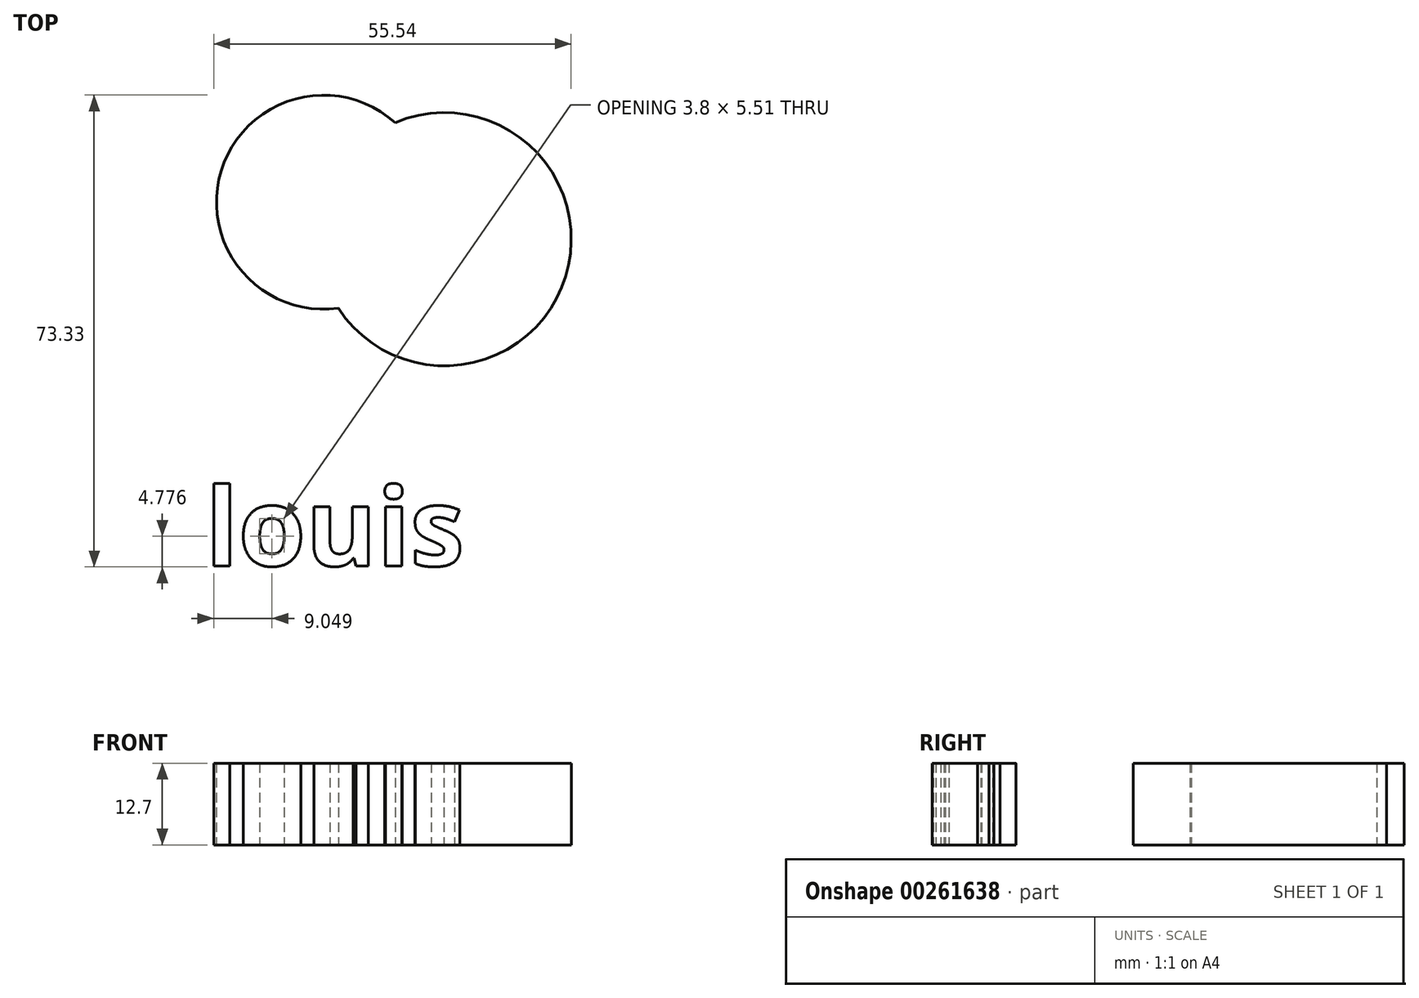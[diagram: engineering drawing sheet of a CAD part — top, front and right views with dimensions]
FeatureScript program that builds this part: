
annotation { "Feature Type Name" : "Feature", "Feature Type Description" : "" }
export const myFeature = defineFeature(function(context is Context, id is Id, definition is map)
    precondition{}
    {
        {
            var Q0;
            Q0=qCreatedBy(makeId("Top.planeOp"),FACE);
            var sketch = newSketch(context, id + "F0", { "sketchPlane" : qUnion([Q0])});
            skCircle(sketch, "E0", {"center": v(-6.81, 12.7) * mm, "radius": 19.68 * mm});
            skCircle(sketch, "E1", {"center": v(-25.62, 18.47) * mm, "radius": 16.63 * mm});
            skText(sketch, "E2", { "text": "louis\n", "fontName": "OpenSans-Bold.ttf"});
            const initialGuessF0  = {"E2": [-0.044, -0.03805, 1, 0, 0.01215]};
            skSetInitialGuess(sketch, initialGuessF0);
            skSolve(sketch);
        }
        {
            var Q0;
            Q0 = qSketchRegion(id + "F0", true);
            extrude(context, id + "F1", {"entities" : qUnion([Q0]), "depth" : 12.7 * mm});
        }
    });
